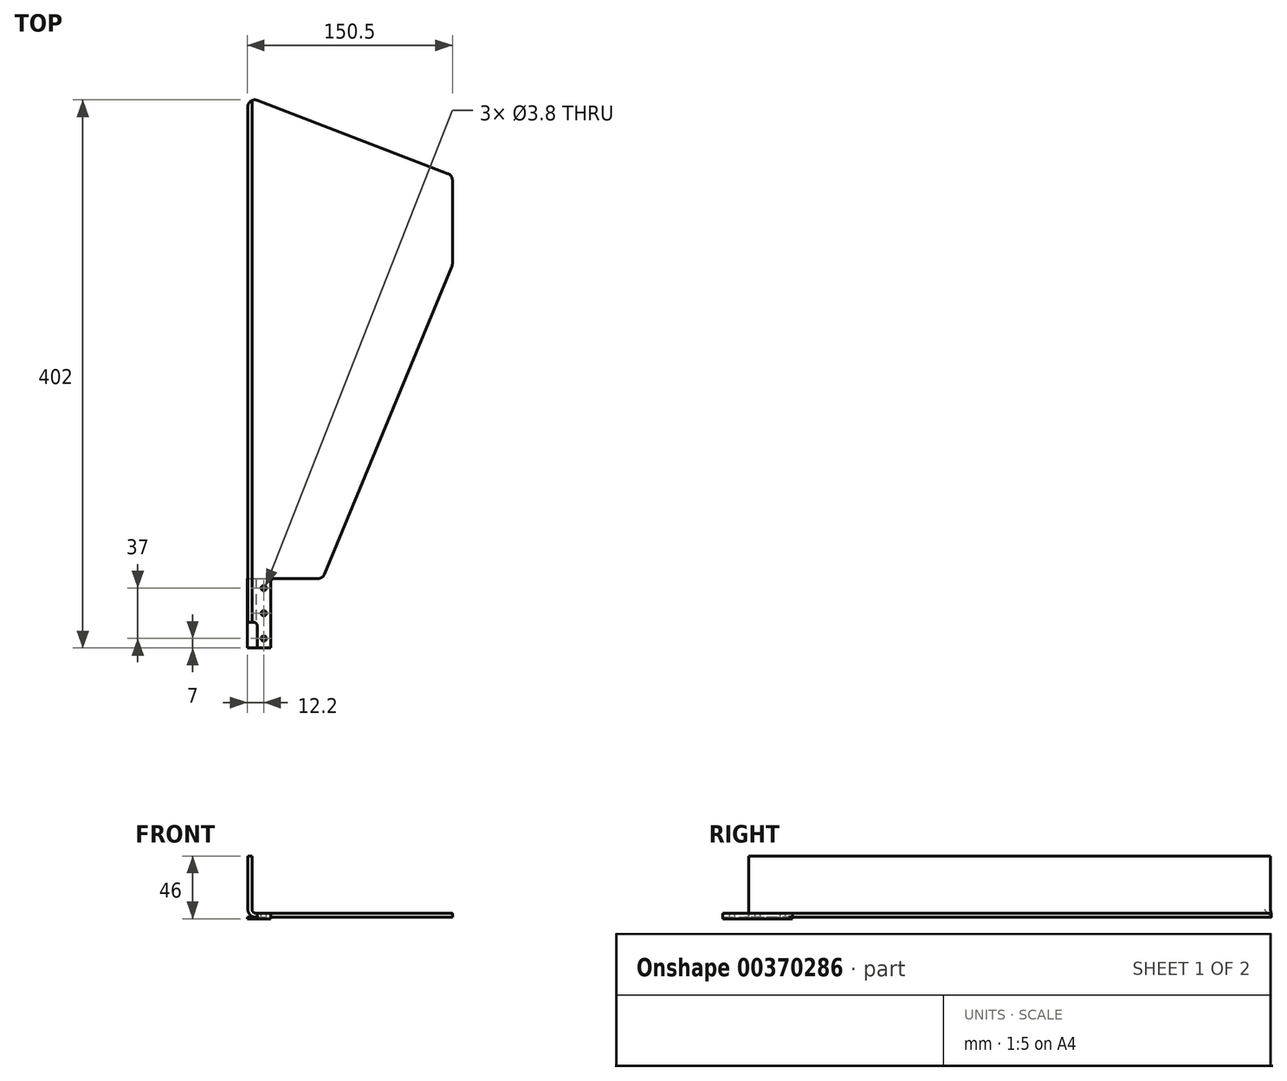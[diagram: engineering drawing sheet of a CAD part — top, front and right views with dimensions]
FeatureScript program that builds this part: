
annotation { "Feature Type Name" : "Feature", "Feature Type Description" : "" }
export const myFeature = defineFeature(function(context is Context, id is Id, definition is map)
    precondition{}
    {
        {
            var Q0;
            Q0=qCreatedBy(makeId("Front.planeOp"),FACE);
            var sketch = newSketch(context, id + "F0", { "sketchPlane" : qUnion([Q0])});
            skLineSegment(sketch, "E0", {"start": v(-20, 42) * mm, "end": v(-20, 3) * mm});
            skLineSegment(sketch, "E1", {"start": v(-17, 0) * mm, "end": v(127, 0) * mm});
            skPoint(sketch, "E2", {"position": v(0, 0) * mm});
            skPoint(sketch, "E3.visualSharp", {"position": v(-20, 0) * mm});
            skArc(sketch, "E3.filletArc", {"start": v(-20, 3) * mm, "mid": v(-19.12, 0.88) * mm, "end": v(-17, 0) * mm});
            skLineSegment(sketch, "E4", {"start": v(-20, 42) * mm, "end": v(-23, 42) * mm});
            skLineSegment(sketch, "E5", {"start": v(-23, 42) * mm, "end": v(-23, 3) * mm});
            skLineSegment(sketch, "E6", {"start": v(-17, -3) * mm, "end": v(127, -3) * mm});
            skPoint(sketch, "E7.visualSharp", {"position": v(-23, -3) * mm});
            skArc(sketch, "E7.filletArc", {"start": v(-23, 3) * mm, "mid": v(-21.24, -1.24) * mm, "end": v(-17, -3) * mm});
            skLineSegment(sketch, "E8", {"start": v(127, 0) * mm, "end": v(127, -3) * mm});
            skSolve(sketch);
        }
        {
            var Q0;
            Q0=qSketchRegion(id+"F0",true);
            extrude(context, id + "F1", {"entities" : qUnion([Q0]), "oppositeDirection" : true, "depth" : 500 * mm});
        }
        {
            var Q0;
            Q0=qCreatedBy(makeId("Top.planeOp"),FACE);
            var sketch = newSketch(context, id + "F2", { "sketchPlane" : qUnion([Q0])});
            skLineSegment(sketch, "E9.bottom", {"start": v(-56.37, 525.22) * mm, "end": v(165.37, 525.22) * mm});
            skLineSegment(sketch, "E9.top", {"start": v(-56.37, -13.1) * mm, "end": v(165.37, -13.1) * mm});
            skLineSegment(sketch, "E9.left", {"start": v(-56.37, 525.22) * mm, "end": v(-56.37, -13.1) * mm});
            skLineSegment(sketch, "E9.right", {"start": v(165.37, 525.22) * mm, "end": v(165.37, -13.1) * mm});
            skLineSegment(sketch, "E10.bottom", {"start": v(455.61, 344.43) * mm, "end": v(485.6, 345.09) * mm});
            skLineSegment(sketch, "E10.top", {"start": v(456.73, 293.44) * mm, "end": v(486.72, 294.1) * mm});
            skLineSegment(sketch, "E10.left", {"start": v(455.61, 344.43) * mm, "end": v(456.73, 293.44) * mm});
            skLineSegment(sketch, "E10.right", {"start": v(485.6, 345.09) * mm, "end": v(486.72, 294.1) * mm});
            skCircle(sketch, "E11", {"center": v(481.57, 300.99) * mm, "radius": 1.9 * mm});
            skCircle(sketch, "E12", {"center": v(480.76, 337.98) * mm, "radius": 1.9 * mm});
            skCircle(sketch, "E13", {"center": v(460.77, 337.54) * mm, "radius": 1.9 * mm});
            skCircle(sketch, "E14", {"center": v(461.57, 300.55) * mm, "radius": 1.9 * mm});
            skPoint(sketch, "E15", {"position": v(456.17, 318.94) * mm});
            skLineSegment(sketch, "E16.left", {"start": v(468.41, 344.71) * mm, "end": v(469.52, 293.72) * mm});
            skLineSegment(sketch, "E16.right", {"start": v(472.81, 344.8) * mm, "end": v(473.92, 293.82) * mm});
            skLineSegment(sketch, "E17.0", {"start": v(461.57, 300.55) * mm, "end": v(481.57, 300.99) * mm, "construction": true});
            skLineSegment(sketch, "E18.0", {"start": v(460.77, 337.54) * mm, "end": v(480.76, 337.98) * mm, "construction": true});
            skLineSegment(sketch, "E19.0", {"start": v(461.57, 300.55) * mm, "end": v(460.77, 337.54) * mm, "construction": true});
            skLineSegment(sketch, "E20.0", {"start": v(481.57, 300.99) * mm, "end": v(480.76, 337.98) * mm, "construction": true});
            skPoint(sketch, "E21", {"position": v(470.61, 344.76) * mm});
            skCircle(sketch, "E22", {"center": v(461.17, 319.05) * mm, "radius": 1.9 * mm});
            skCircle(sketch, "E23", {"center": v(481.16, 319.48) * mm, "radius": 1.9 * mm});
            skLineSegment(sketch, "E24", {"start": v(486.72, 294.1) * mm, "end": v(474.92, 293.84) * mm});
            skLineSegment(sketch, "E25", {"start": v(467.41, 344.69) * mm, "end": v(455.61, 344.43) * mm});
            skLineSegment(sketch, "E26.1.3", {"start": v(456.01, 326.28) * mm, "end": v(455.61, 344.43) * mm});
            skPoint(sketch, "E27", {"position": v(510.48, 432.74) * mm});
            skPoint(sketch, "E28.visualSharp", {"position": v(485.6, 345.09) * mm});
            skLineSegment(sketch, "E29", {"start": v(33.19, 54.09) * mm, "end": v(126.62, 279.65) * mm});
            skLineSegment(sketch, "E30", {"start": v(-23, 19) * mm, "end": v(-23, 397) * mm});
            skLineSegment(sketch, "E31", {"start": v(-16.2, 401.67) * mm, "end": v(123.8, 347.93) * mm});
            skLineSegment(sketch, "E32", {"start": v(-6.3, 0) * mm, "end": v(-6.3, 48) * mm});
            skLineSegment(sketch, "E33", {"start": v(-3.3, 51) * mm, "end": v(28.57, 51) * mm});
            skLineSegment(sketch, "E34", {"start": v(-23, 19) * mm, "end": v(-19, 19) * mm});
            skLineSegment(sketch, "E35", {"start": v(-16, 16) * mm, "end": v(-16, 0) * mm});
            skLineSegment(sketch, "E36", {"start": v(-16, 0) * mm, "end": v(-6.3, 0) * mm});
            skLineSegment(sketch, "E37", {"start": v(127, 343.26) * mm, "end": v(127, 281.57) * mm});
            skPoint(sketch, "E38.visualSharp", {"position": v(-23, 404.28) * mm});
            skArc(sketch, "E38.filletArc", {"start": v(-16.2, 401.67) * mm, "mid": v(-20.83, 401.12) * mm, "end": v(-23, 397) * mm});
            skPoint(sketch, "E39.visualSharp", {"position": v(127, 346.7) * mm});
            skArc(sketch, "E39.filletArc", {"start": v(127, 343.26) * mm, "mid": v(126.12, 346.1) * mm, "end": v(123.8, 347.93) * mm});
            skPoint(sketch, "E40.visualSharp", {"position": v(127, 280.57) * mm});
            skArc(sketch, "E40.filletArc", {"start": v(126.62, 279.65) * mm, "mid": v(126.9, 280.6) * mm, "end": v(127, 281.57) * mm});
            skPoint(sketch, "E41.visualSharp", {"position": v(31.9, 51) * mm});
            skArc(sketch, "E41.filletArc", {"start": v(28.57, 51) * mm, "mid": v(31.35, 51.84) * mm, "end": v(33.19, 54.09) * mm});
            skPoint(sketch, "E42.visualSharp", {"position": v(-16, 19) * mm});
            skArc(sketch, "E42.filletArc", {"start": v(-16, 16) * mm, "mid": v(-16.88, 18.12) * mm, "end": v(-19, 19) * mm});
            skArc(sketch, "E43.filletArc", {"start": v(-3.3, 51) * mm, "mid": v(-5.42, 50.12) * mm, "end": v(-6.3, 48) * mm});
            skCircle(sketch, "E44", {"center": v(-11.3, 7) * mm, "radius": 1.9 * mm});
            skCircle(sketch, "E45", {"center": v(-11.3, 44) * mm, "radius": 1.9 * mm});
            skLineSegment(sketch, "E46.0", {"start": v(-11.3, 7) * mm, "end": v(-11.3, 44) * mm, "construction": true});
            skCircle(sketch, "E47", {"center": v(-11.3, 25.5) * mm, "radius": 1.9 * mm});
            skSolve(sketch);
        }
        {
            var Q0;
            Q0=qSketchRegion(id+"F2",true);
            var Q1;
            Q1=makeQuery(id+"F2.imprint","IMPRINT",FACE,{"disambiguationData":[TD([[makeQuery(id+"F2.imprint","IMPRINT",EDGE,{"derivedFrom":sQuery(id+"F2.wireOp",EDGE,"E45")}),1.0]])]});
            var Q2;
            Q2=makeQuery(id+"F2.imprint","IMPRINT",FACE,{"disambiguationData":[TD([[makeQuery(id+"F2.imprint","IMPRINT",EDGE,{"derivedFrom":sQuery(id+"F2.wireOp",EDGE,"E47")}),1.0]])]});
            var Q3;
            Q3=makeQuery(id+"F2.imprint","IMPRINT",FACE,{"disambiguationData":[TD([[makeQuery(id+"F2.imprint","IMPRINT",EDGE,{"derivedFrom":sQuery(id+"F2.wireOp",EDGE,"E44")}),1.0]])]});
            extrude(context, id + "F3", {"entities" : qUnion([Q0, Q1, Q2, Q3]), "operationType" : NewBodyOperationType.REMOVE, "endBound" : BoundingType.SYMMETRIC, "oppositeDirection" : true, "depth" : 100 * mm});
        }
        {
            var Q0;
            Q0=makeQuery(id+"F1.opExtrude","SWEPT_FACE",FACE,{"disambiguationData":[OSD([sQuery(id+"F0.wireOp",EDGE,"E6")])]});
            var sketch = newSketch(context, id + "F4", { "sketchPlane" : qUnion([Q0])});
            skLineSegment(sketch, "E48.bottom", {"start": v(-23.5, 0) * mm, "end": v(-6.3, 0) * mm});
            skLineSegment(sketch, "E48.top", {"start": v(-23.5, -51) * mm, "end": v(-6.3, -51) * mm});
            skLineSegment(sketch, "E48.right", {"start": v(-6.3, 0) * mm, "end": v(-6.3, -51) * mm});
            skCircle(sketch, "E49", {"center": v(-11.3, -44) * mm, "radius": 1.9 * mm});
            skCircle(sketch, "E50", {"center": v(-11.3, -7) * mm, "radius": 1.9 * mm});
            skLineSegment(sketch, "E51.left", {"start": v(-23.5, 0) * mm, "end": v(-23.5, -51) * mm});
            skLineSegment(sketch, "E51.right", {"start": v(-19.1, 0) * mm, "end": v(-19.1, -51) * mm});
            skLineSegment(sketch, "E52.0", {"start": v(-11.3, -44) * mm, "end": v(-11.3, -7) * mm, "construction": true});
            skCircle(sketch, "E53", {"center": v(-11.3, -25.5) * mm, "radius": 1.9 * mm});
            skPoint(sketch, "E54.visualSharp", {"position": v(-6.3, 0) * mm});
            skSolve(sketch);
        }
        {
            var Q0;
            Q0 = qSketchRegion(id + "F4", true);
            extrude(context, id + "F5", {"entities" : qUnion([Q0]), "operationType" : NewBodyOperationType.ADD, "depth" : 1 * mm});
        }
    });
